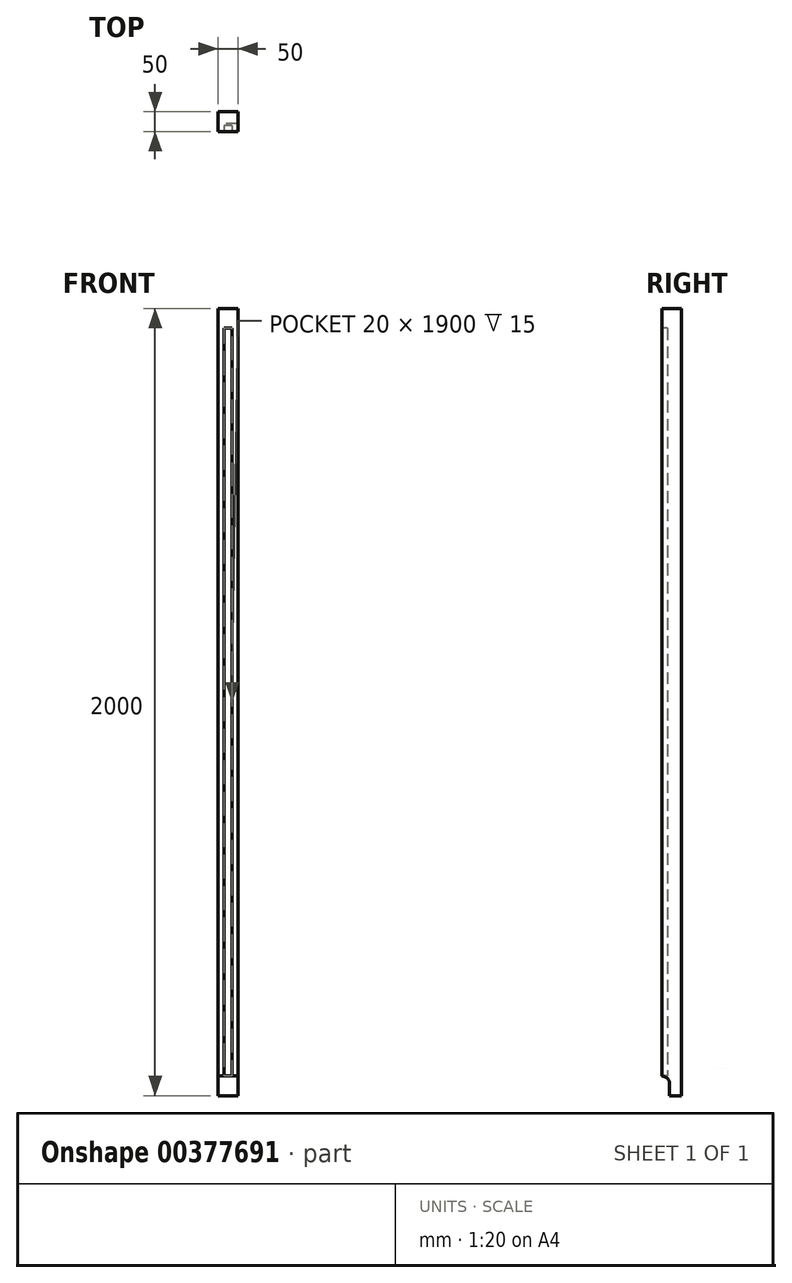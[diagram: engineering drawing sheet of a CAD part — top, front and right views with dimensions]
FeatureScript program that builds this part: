
annotation { "Feature Type Name" : "Feature", "Feature Type Description" : "" }
export const myFeature = defineFeature(function(context is Context, id is Id, definition is map)
    precondition{}
    {
        {
            var Q0;
            Q0=qCreatedBy(makeId("Top.planeOp"),FACE);
            var sketch = newSketch(context, id + "F0", { "sketchPlane" : qUnion([Q0])});
            skLineSegment(sketch, "E0.bottom", {"start": v(0, 0) * mm, "end": v(50, 0) * mm});
            skLineSegment(sketch, "E0.top", {"start": v(0, 50) * mm, "end": v(50, 50) * mm});
            skLineSegment(sketch, "E0.left", {"start": v(0, 0) * mm, "end": v(0, 50) * mm});
            skLineSegment(sketch, "E0.right", {"start": v(50, 0) * mm, "end": v(50, 50) * mm});
            skSolve(sketch);
        }
        {
            var Q0;
            Q0=makeQuery(id+"F0.imprint","IMPRINT",FACE,{"disambiguationData":[TD([[makeQuery(id+"F0.imprint","IMPRINT",EDGE,{"derivedFrom":sQuery(id+"F0.wireOp",EDGE,"E0.bottom")}),1.0]])]});
            extrude(context, id + "F1", {"entities" : qUnion([Q0]), "depth" : 2000 * mm});
        }
        {
            var Q0;
            Q0=qCreatedBy(makeId("Front.planeOp"),FACE);
            var sketch = newSketch(context, id + "F2", { "sketchPlane" : qUnion([Q0])});
            skLineSegment(sketch, "E1.bottom", {"start": v(35, 1950) * mm, "end": v(15, 1950) * mm});
            skLineSegment(sketch, "E1.top", {"start": v(35, 50) * mm, "end": v(15, 50) * mm});
            skLineSegment(sketch, "E1.left", {"start": v(35, 1950) * mm, "end": v(35, 50) * mm});
            skLineSegment(sketch, "E1.right", {"start": v(15, 1950) * mm, "end": v(15, 50) * mm});
            skSolve(sketch);
        }
        {
            var Q0;
            Q0=makeQuery(id+"F2.imprint","IMPRINT",FACE,{"disambiguationData":[TD([[makeQuery(id+"F2.imprint","IMPRINT",EDGE,{"derivedFrom":sQuery(id+"F2.wireOp",EDGE,"E1.bottom")}),1.0]])]});
            extrude(context, id + "F3", {"entities" : qUnion([Q0]), "operationType" : NewBodyOperationType.REMOVE, "oppositeDirection" : true, "depth" : 15 * mm});
        }
        {
            var Q0;
            Q0=qCreatedBy(makeId("Right.planeOp"),FACE);
            var sketch = newSketch(context, id + "F4", { "sketchPlane" : qUnion([Q0])});
            skLineSegment(sketch, "E2.bottom", {"start": v(0, 0) * mm, "end": v(20, 0) * mm});
            skLineSegment(sketch, "E2.top", {"start": v(0, 50) * mm, "end": v(0, 50) * mm});
            skLineSegment(sketch, "E2.left", {"start": v(0, 0) * mm, "end": v(0, 50) * mm});
            skLineSegment(sketch, "E2.right", {"start": v(20, 0) * mm, "end": v(20, 30) * mm});
            skPoint(sketch, "E3.visualSharp", {"position": v(20, 50) * mm});
            skArc(sketch, "E3.filletArc", {"start": v(20, 30) * mm, "mid": v(14.14, 44.14) * mm, "end": v(0, 50) * mm});
            skSolve(sketch);
        }
        {
            var Q0;
            Q0=makeQuery(id+"F4.imprint","IMPRINT",FACE,{"disambiguationData":[TD([[makeQuery(id+"F4.imprint","IMPRINT",EDGE,{"derivedFrom":sQuery(id+"F4.wireOp",EDGE,"E2.bottom")}),1.0]])]});
            extrude(context, id + "F5", {"entities" : qUnion([Q0]), "operationType" : NewBodyOperationType.REMOVE, "endBound" : BoundingType.THROUGH_ALL, "depth" : 25 * mm});
        }
    });
